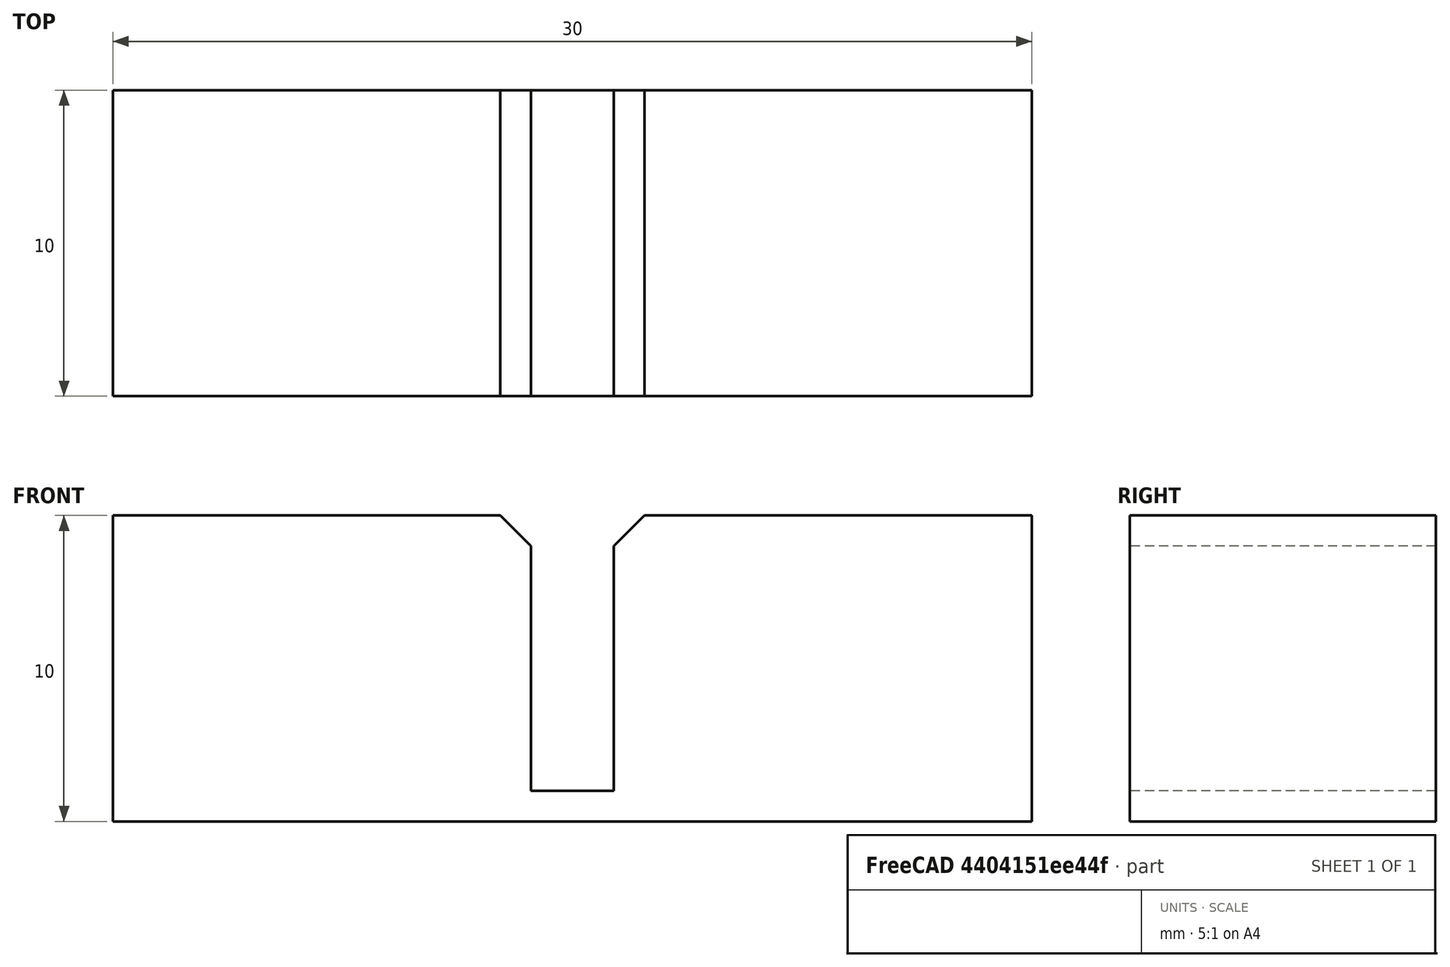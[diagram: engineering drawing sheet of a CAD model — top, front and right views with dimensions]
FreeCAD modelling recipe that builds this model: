
FCSTD DOCUMENT  (FreeCAD 0.20R29603 (Git))
Label: callout-for-pcb-0009-05
License: Other
objects: TechDraw::DrawViewDimension×4, Sketcher::SketchObject×1, PartDesign::Pad×1, PartDesign::Pocket×1, PartDesign::Body×1, TechDraw::DrawSVGTemplate×1, TechDraw::DrawViewPart×1, TechDraw::DrawPage×1
note: 6 computed .brp shape members not serialized (recipe doc carries the construction recipe); baked Part::Feature solids carry a one-line shape summary decoded from their .brp

FEATURE [Sketcher::SketchObject] Sketch
  FullyConstrained = true
  MapMode = 5
  Placement = pos=(0,0,0) rot=(1,0,0;1.5708rad)
  Support = -> [XZ_Plane]
  sketch-geometry (10):
    g0: LineSegment StartX=-2.35 StartY=1 StartZ=0 EndX=-1.35 EndY=1e-16 EndZ=0
    g1: LineSegment StartX=1.35 StartY=-2e-16 StartZ=0 EndX=2.35 EndY=1 EndZ=0
    g2: LineSegment StartX=-1.35 StartY=1e-16 StartZ=0 EndX=-1.35 EndY=0 EndZ=0
    g3: LineSegment StartX=1.35 StartY=0 StartZ=0 EndX=1.35 EndY=-2e-16 EndZ=0
    g4: LineSegment StartX=-2.35 StartY=1 StartZ=0 EndX=-15 EndY=1 EndZ=0
    g5: LineSegment StartX=2.35 StartY=1 StartZ=0 EndX=15 EndY=1 EndZ=0
    g6: LineSegment StartX=-15 StartY=1 StartZ=0 EndX=-15 EndY=-9 EndZ=0
    g7: LineSegment StartX=-15 StartY=-9 StartZ=0 EndX=15 EndY=-9 EndZ=0
    g8: LineSegment StartX=15 StartY=-9 StartZ=0 EndX=15 EndY=1 EndZ=0
    g9: LineSegment StartX=-1.35 StartY=1e-16 StartZ=0 EndX=1.35 EndY=-2e-16 EndZ=0
  constraints (28):
    c: Symmetric(g0,g1,g-2)
    c: Angle(g1,g0) = 1.5708
    c: PointOnObject(g2,g-1)
    c: Vertical(g2)
    c: Vertical(g3)
    c: Symmetric(g2,g3,g-2)
    c: Coincident(g4,g0)
    c: Horizontal(g4)
    c: Coincident(g5,g1)
    c: Horizontal(g5)
    c: Coincident(g1,g3)
    c: Coincident(g0,g2)
    c: Distance(g0,g1) = 4.7
    c: Equal(g0,g1)
    c: DistanceX(g0,g1) = 2.7
    c: DistanceY(g0,g0) = 1
    c: PointOnObject(g0,g-1)
    c: Vertical(g6)
    c: Coincident(g7,g6)
    c: Coincident(g8,g7)
    c: Vertical(g8)
    c: Symmetric(g6,g7,g-2)
    c: Coincident(g4,g6)
    c: Coincident(g5,g8)
    c: Coincident(g9,g0)
    c: Coincident(g9,g1)
    c: DistanceY(g8,g8) = 10
    c: DistanceX(g7,g7) = 30
FEATURE [PartDesign::Pad] Pad
  Direction = (0,-1,2e-16)
  Length = 10
  Length2 = 10
  Placement = pos=(0,0,0) rot=(1,0,0;1.5708rad)
  Profile = -> Sketch
  ReferenceAxis = -> Sketch [N_Axis]
  Type = 0
FEATURE [PartDesign::Pocket] Pocket
  BaseFeature = -> Pad
  Direction = (-1e-16,-2e-16,-1)
  Length = 8
  Length2 = 5
  Placement = pos=(0,0,0) rot=(1,0,0;1.5708rad)
  Profile = -> Pad [Face4]
  Type = 0
FEATURE [PartDesign::Body] Body
  Group = -> [Sketch,Pad,Pocket]
  Origin = -> Origin
  Tip = -> Pocket
FEATURE [TechDraw::DrawSVGTemplate] Template
  EditableTexts = Designed_by_Name=Designed by Name; Drawing_number=Drawing number; FC-Date=Date; FC-SC=Scale; FC-SH=Sheet; FC-Title=Title; Subtitle=Subtitle; Weight=Weight
  Height = 210
  Orientation = 1
  Width = 297
FEATURE [TechDraw::DrawViewPart] View
  CoarseView = false
  Direction = (0,-1,0)
  Focus = 100
  HardHidden = false
  IsoCount = 0
  IsoHidden = false
  IsoVisible = false
  LockPosition = false
  Perspective = false
  Rotation = 0
  Scale = 6
  ScaleType = 2
  SeamHidden = false
  SeamVisible = true
  SmoothHidden = false
  SmoothVisible = true
  Source = -> [Pocket]
  X = 146.933
  XDirection = (1,0,0)
  Y = 109.592
FEATURE [TechDraw::DrawViewDimension] Dimension
  AngleOverride = false
  Arbitrary = false
  ArbitraryTolerances = false
  EqualTolerance = true
  ExtensionAngle = 0
  FormatSpec = %.2w
  FormatSpecOverTolerance = %+.2w
  FormatSpecUnderTolerance = %+.2w
  Inverted = false
  LineAngle = 0
  LockPosition = false
  MeasureType = 1
  OverTolerance = 0
  References2D = -> [View]
  Rotation = 0
  ScaleType = 2
  TheoreticalExact = false
  Type = 6
  UnderTolerance = 0
  X = -37.6545
  Y = 69.3538
FEATURE [TechDraw::DrawViewDimension] Dimension001
  AngleOverride = false
  Arbitrary = false
  ArbitraryTolerances = false
  EqualTolerance = true
  ExtensionAngle = 0
  FormatSpec = %.2w
  FormatSpecOverTolerance = %+.2w
  FormatSpecUnderTolerance = %+.2w
  Inverted = false
  LineAngle = 0
  LockPosition = false
  MeasureType = 1
  OverTolerance = 0
  References2D = -> [View]
  Rotation = 0
  ScaleType = 2
  TheoreticalExact = false
  Type = 2
  UnderTolerance = 0
  X = -1.07024
  Y = 43.0798
FEATURE [TechDraw::DrawViewDimension] Dimension002
  AngleOverride = false
  Arbitrary = false
  ArbitraryTolerances = false
  EqualTolerance = true
  ExtensionAngle = 0
  FormatSpec = %.2w
  FormatSpecOverTolerance = %+.2w
  FormatSpecUnderTolerance = %+.2w
  Inverted = false
  LineAngle = 0
  LockPosition = false
  MeasureType = 1
  OverTolerance = 0
  References2D = -> [View]
  Rotation = 0
  ScaleType = 2
  TheoreticalExact = false
  Type = 1
  UnderTolerance = 0
  X = 21.1674
  Y = 52.5129
FEATURE [TechDraw::DrawViewDimension] Dimension003
  AngleOverride = false
  Arbitrary = false
  ArbitraryTolerances = false
  EqualTolerance = true
  ExtensionAngle = 0
  FormatSpec = %.2w
  FormatSpecOverTolerance = %+.2w
  FormatSpecUnderTolerance = %+.2w
  Inverted = false
  LineAngle = 0
  LockPosition = false
  MeasureType = 1
  OverTolerance = 0
  References2D = -> [View]
  Rotation = 0
  ScaleType = 2
  TheoreticalExact = false
  Type = 1
  UnderTolerance = 0
  X = 29.2605
  Y = 60.0913
FEATURE [TechDraw::DrawPage] Page
  KeepUpdated = true
  NextBalloonIndex = 1
  ProjectionType = 0
  Template = -> Template
  Views = -> [View,Dimension,Dimension001,Dimension002,Dimension003]
